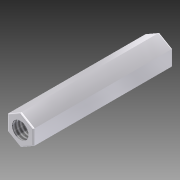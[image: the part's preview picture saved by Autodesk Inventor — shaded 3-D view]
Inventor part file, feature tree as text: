
AUTODESK INVENTOR PART (.ipt)
format: ipt  version: 2012 (Build 160160000, 160)  size: 98,816 bytes
history: native  units: in
note: dims shown in document units (in); Inventor stores cm internally (conversion verified against a paired STEP export)
features: fillet x2, extrude x1, thread x1, sketch x1
ambient origin geometry x8: Origin, YZ Plane, XZ Plane, XY Plane, X Axis, Y Axis, Z Axis, Center Point
bodies: Solid1 (feature_tree)
feature tree (5):
  extrude  "Extrusion1"  Depth=1.0in TaperAngle=0.0deg
  fillet  "Fillet1"  Radius=0.01in
  fillet  "Fillet2"  Radius=0.01in
  thread  "Thread1"  [1 undecoded]
  sketch  "Sketch1"  dims[d1=0.118in d2=1.0in d3=0.0in d4=0.01in d5=0.01in d6=1.0in d7=0.0in]
note: 1 required parameter value undecoded (feature->parameter linkage not recoverable at this tier; creation-order binding heuristic only, values carry confidence <= 0.55)
